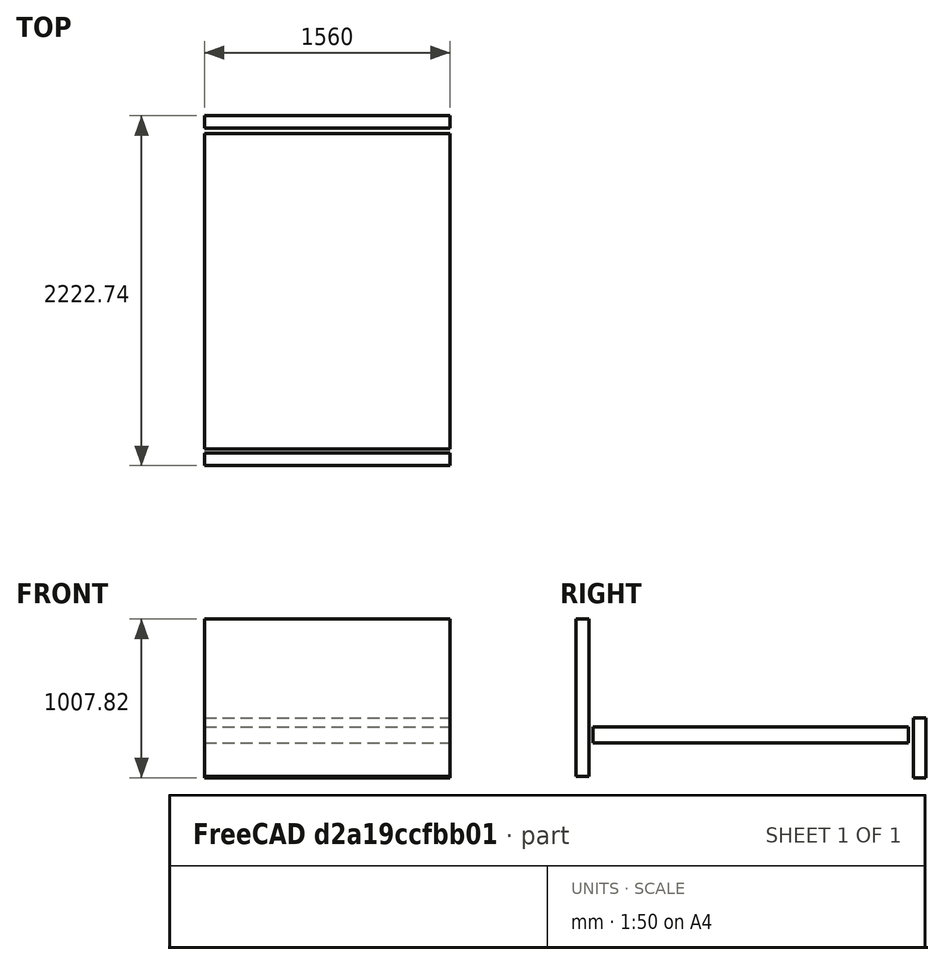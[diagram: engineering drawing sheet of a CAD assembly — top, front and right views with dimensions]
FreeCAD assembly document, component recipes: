
FREECAD ASSEMBLY — COMPONENT RECIPES ("mueble_con_ensamblaje")

This assembly document has 3 components, labeled P0..P2 below (a component is one placed body or linked part). 0 of them carry a construction recipe — the FreeCAD feature program that regenerates the part from scratch, quoted from this document or its linked companion documents; the rest are supplied as boundary geometry only. No exploded tour is included for this assembly.
COMPONENT P0 — geometry summary ("cabecero"; no construction recipe available for this part):
  bounding box: 1560.0 x 1000.0 x 80.0 mm
  tessellated surface: 12 triangles
  volume: 124800000 mm^3 (100% of its bounding box)
  symmetry: 2-fold rotationally symmetric about the x axis; 2-fold rotationally symmetric about the z axis; mirror-symmetric across its x mid-plane, y mid-plane, z mid-plane
COMPONENT P1 — geometry summary ("pies_de_la_cama"; no construction recipe available for this part):
  bounding box: 1560.0 x 380.0 x 80.0 mm
  tessellated surface: 12 triangles
  volume: 47424000 mm^3 (100% of its bounding box)
  symmetry: 2-fold rotationally symmetric about the y axis; 2-fold rotationally symmetric about the z axis; mirror-symmetric across its x mid-plane, y mid-plane, z mid-plane
COMPONENT P2 — geometry summary ("armadura"; no construction recipe available for this part):
  bounding box: 2004.0 x 1560.0 x 100.0 mm
  tessellated surface: 12 triangles
  volume: 312624000 mm^3 (100% of its bounding box)
  symmetry: 2-fold rotationally symmetric about the x axis; 2-fold rotationally symmetric about the y axis; 2-fold rotationally symmetric about the z axis; mirror-symmetric across its x mid-plane, y mid-plane, z mid-plane
PROVENANCE & LICENSES
A FreeCAD (.FCStd) document from a public repository crawl; recipes are the document's own serialized feature recipes (and, for linked parts, companion documents' recipes).
License: gpl-3.0.
